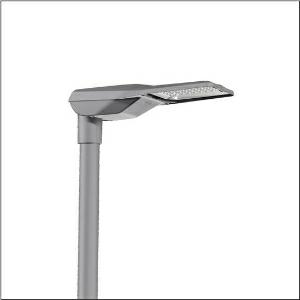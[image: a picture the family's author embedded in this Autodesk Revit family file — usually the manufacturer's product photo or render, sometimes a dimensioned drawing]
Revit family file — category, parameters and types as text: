
# Revit family: streetlight_sl_21_iq_mini___p1_0a_5xe2a41d08gb_135c
name_source: partatom
category: Lighting Fixtures
units: mm (PartAtom-declared; Revit-internal decimal feet)

## family parameters
Cut with Voids When Loaded = No
Host = Face
Light Source = No
Part Type = Normal
Room Calculation Point = No
Round Connector Dimension = Use Diameter
Shared = No

## types (1)
- --- (1 x LED, 5920 lm, 37.1 W, 4000K)
    Apparent Load = 37 VA
    CIE Flux Codes = 21 50 90 100 100
    Color Rendering = 70
    Color Temperature = 4000K
    Default Elevation = 1800 mm
    Description = Streetlight SL 21 iQ mini, mast luminaire, primary light control with lens, of PMMA, primary optical cover: cover, of toughened safety glass, transparent, light distribution: P1.0a, light emission: direct distribution, primary light characteristic: asymmetric, installation type: post-top, side-entry, LED, High Power LED, rated luminous flux: 5.920lm, luminous efficacy: 160lm/W, light colour: 740, colour temperature: 4000K, control gear: iQ-Comfort, control: Auto-Match, Temp-Guard, Lumen-Switch, Night-Set, Smart-Wire, Light-Fading, Desk-Remote (wireless, voltage-free reading and setting of iQ features in the workshop via application-optimized NFC function/RFID function), optimised constant luminous flux control (CLO 2.0), pre-setting: linear dimming characteristic, mains connection: 220..240V, AC, 50/60Hz, start of lifetime: 37W, end of service life: 39W, reduction: 18W, luminaire housing, of diecast aluminium, powder-coated, SITECO metallic grey (DB 702S), corrosivity category C5 high according to DIN EN ISO 12944, please order mast flange separately, inclination adjustable: 0°, 5°, 10°, 15°, sealing non-destructively replaceable, multi-level sealing system, length: 628mm, width: 235mm, height: 110mm, mast flange for spigot size: 42mm (side-entry): 5XC10008XM4, 60/48mm (side-entry/post-top): 5XC10108XM2, 76/60mm (side-entry/post-top): 5XC10108XM1, mounting height: 4..8m, protection rating (complete): IP66, insulation class (complete): insulation class II (safety insulation), certification: CE, ENEC, ENEC+, VDE, impact resistance: IK10, permissible operating ambient temperature for outdoor applications: -40..+50°C, standard-compliant lighting for roads and squares, packaging unit: 1 piece

Light Distribution: P1.0a
    Height = 110 mm
    Lamp = 1 x LED
    Lamp Light Flux = 5920 lm
    Lamp Power = 37.1 W
    Lamp count = 1
    Length = 625 mm
    Luminous efficacy = 160 lm/W
    Manufacturer = Siteco
    ModVariant = No
    Model = 5XE2A41D08GB
    Number of Poles = 1
    OnlyDefault = Yes
    Power Factor = 1
    Product Name = Streetlight SL 21 iQ mini | P1.0a
    Product group = mast luminaire | pylon top
    ProductGroupID = 6100
    Protection Class = Protection class II
    Protection Degree = IP 66
    RLX_Detail_Level = 1
    RLX_Emergency_Light_Flux = 0 lm
    RLX_Emergency_Type = 0
    RLX_Emergency_Type_DB = No
    RlxData = <blob elided: 37529 chars, md5=b4542b01>
    Socket = socket
    Standby Power = 0 W
    System Light Flux = 5920 lm
    System Power = 37 W
    Type Comments = factory setting: luminous flux: 100 % | dim-lin: 254 | 385 mA
    Type Image = l_1003519.jpg
    URL = http://relux.com
    VarID = @adj_184241
    Voltage = 0 V
    Weight = 0.00 kg
    Width = 234 mm

## geometry (parser evidence)
native form markers: Blend x4, Sweep x11
no freeform markers — native parametric forms only
